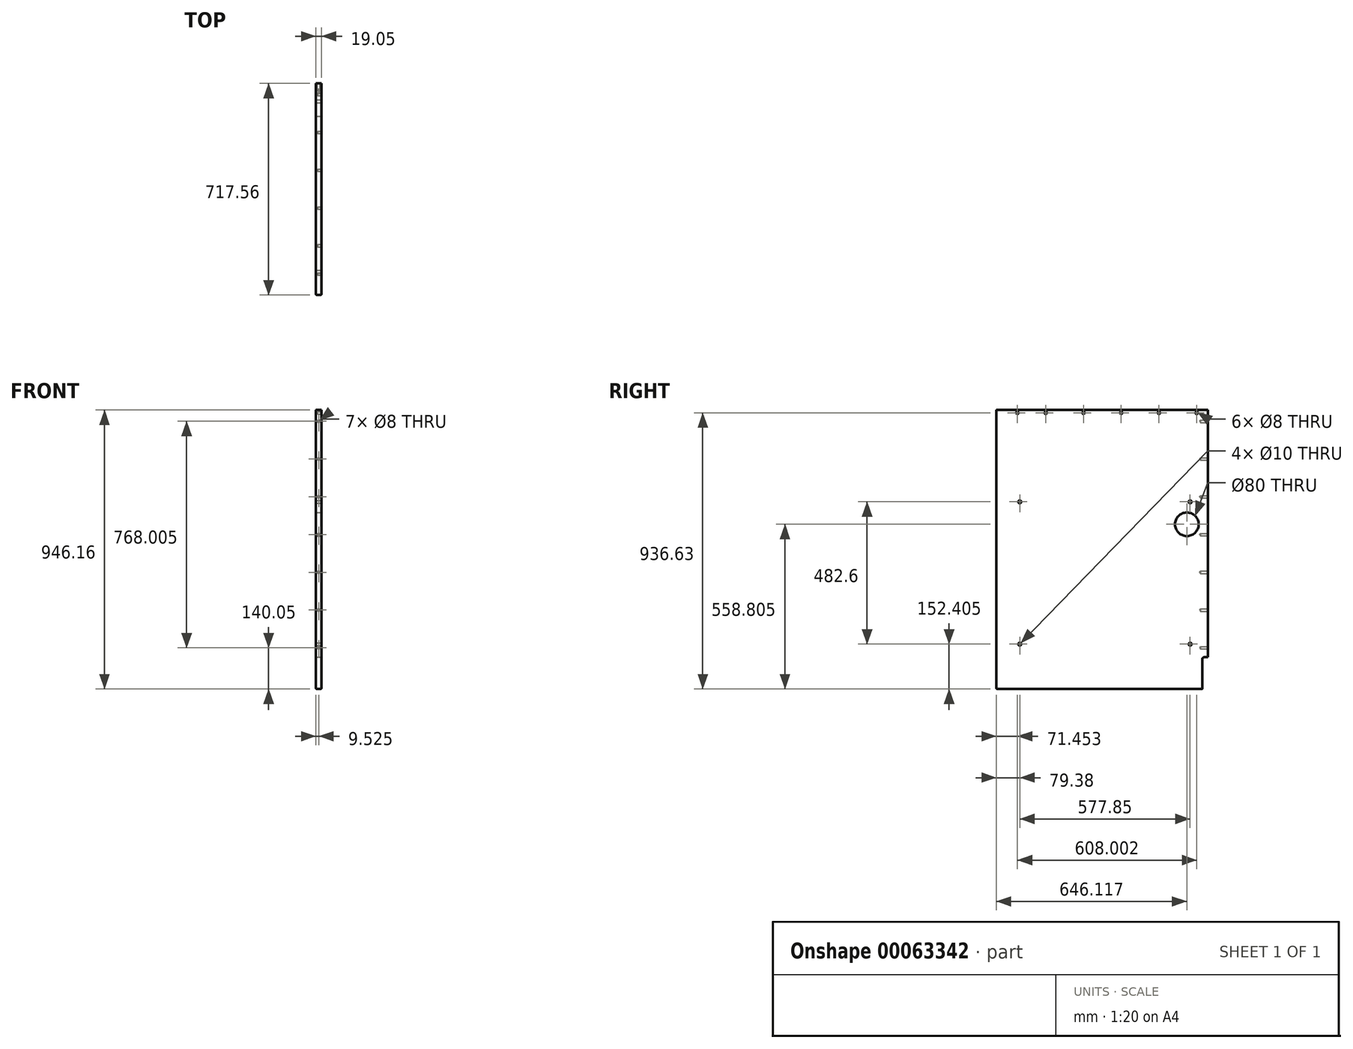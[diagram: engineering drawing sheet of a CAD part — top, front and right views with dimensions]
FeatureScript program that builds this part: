
annotation { "Feature Type Name" : "Feature", "Feature Type Description" : "" }
export const myFeature = defineFeature(function(context is Context, id is Id, definition is map)
    precondition{}
    {
        {
            var Q0;
            Q0=qCreatedBy(makeId("Right.planeOp"),FACE);
            var sketch = newSketch(context, id + "F0", { "sketchPlane" : qUnion([Q0])});
            skLineSegment(sketch, "E0.rect.bottom", {"start": v(358.78, -473.08) * mm, "end": v(-358.78, -473.08) * mm});
            skLineSegment(sketch, "E0.rect.top", {"start": v(358.78, 473.08) * mm, "end": v(-358.77, 473.07) * mm});
            skLineSegment(sketch, "E0.rect.left", {"start": v(358.78, -473.08) * mm, "end": v(358.78, 473.08) * mm});
            skLineSegment(sketch, "E0.rect.right", {"start": v(-358.78, -473.08) * mm, "end": v(-358.77, 473.08) * mm});
            skPoint(sketch, "E0.rect.middle", {"position": v(0, 0) * mm});
            skSolve(sketch);
        }
        {
            var Q0;
            Q0=makeQuery(id+"F0.imprint","IMPRINT",FACE,{"disambiguationData":[TD([[makeQuery(id+"F0.imprint","IMPRINT",EDGE,{"derivedFrom":sQuery(id+"F0.wireOp",EDGE,"E0.rect.bottom")}),-1.0]])]});
            extrude(context, id + "F1", {"entities" : qUnion([Q0]), "oppositeDirection" : true, "depth" : 19.05 * mm});
        }
        {
            var Q0;
            Q0=makeQuery(id+"F1.opExtrude","CAP_FACE",FACE,{"disambiguationData":[OSD([sQuery(id+"F0.wireOp",EDGE,"E0.rect.bottom"),sQuery(id+"F0.wireOp",EDGE,"E0.rect.top"),sQuery(id+"F0.wireOp",EDGE,"E0.rect.left"),sQuery(id+"F0.wireOp",EDGE,"E0.rect.right")])],"isStart":true});
            var sketch = newSketch(context, id + "F2", { "sketchPlane" : qUnion([Q0])});
            skPoint(sketch, "E1", {"position": v(320.68, 463.55) * mm});
            skPoint(sketch, "E2", {"position": v(192.67, 463.55) * mm});
            skPoint(sketch, "E3", {"position": v(64.67, 463.55) * mm});
            skPoint(sketch, "E4", {"position": v(-63.33, 463.55) * mm});
            skPoint(sketch, "E5", {"position": v(-191.33, 463.55) * mm});
            skPoint(sketch, "E6", {"position": v(-287.33, 463.55) * mm});
            skSolve(sketch);
        }
        {
            var Q0;
            Q0=sQuery(id+"F2.wireOp",VERTEX,"E6");
            var Q1;
            Q1=sQuery(id+"F2.wireOp",VERTEX,"E5");
            var Q2;
            Q2=sQuery(id+"F2.wireOp",VERTEX,"E4");
            var Q3;
            Q3=sQuery(id+"F2.wireOp",VERTEX,"E3");
            var Q4;
            Q4=sQuery(id+"F2.wireOp",VERTEX,"E2");
            var Q5;
            Q5=sQuery(id+"F2.wireOp",VERTEX,"E1");
            var Q6;
            Q6=makeQuery(id+"F1.opExtrude","SWEPT_BODY",BODY,{"disambiguationData":[OSD([sQuery(id+"F0.wireOp",EDGE,"E0.rect.bottom"),sQuery(id+"F0.wireOp",EDGE,"E0.rect.top"),sQuery(id+"F0.wireOp",EDGE,"E0.rect.left"),sQuery(id+"F0.wireOp",EDGE,"E0.rect.right")])]});
            hole(context, id + "F3", {"style" : HoleStyle.SIMPLE, "holeDiameter" : 8 * mm, "endStyle" : HoleEndStyle.BLIND, "holeDepth" : 12.7 * mm, "locations" : qUnion([Q0, Q1, Q2, Q3, Q4, Q5]), "scope" : qUnion([Q6])});
        }
        {
            var Q0;
            Q0=makeQuery(id+"F1.opExtrude","CAP_FACE",FACE,{"disambiguationData":[OSD([sQuery(id+"F0.wireOp",EDGE,"E0.rect.bottom"),sQuery(id+"F0.wireOp",EDGE,"E0.rect.top"),sQuery(id+"F0.wireOp",EDGE,"E0.rect.left"),sQuery(id+"F0.wireOp",EDGE,"E0.rect.right")])],"isStart":true});
            var sketch = newSketch(context, id + "F4", { "sketchPlane" : qUnion([Q0])});
            skLineSegment(sketch, "E7.bottom", {"start": v(358.78, -473.08) * mm, "end": v(339.73, -473.08) * mm});
            skLineSegment(sketch, "E7.top", {"start": v(358.78, -365.13) * mm, "end": v(346.08, -365.13) * mm});
            skLineSegment(sketch, "E7.left", {"start": v(358.78, -473.08) * mm, "end": v(358.78, -365.13) * mm});
            skLineSegment(sketch, "E7.right", {"start": v(339.73, -473.08) * mm, "end": v(339.73, -371.48) * mm});
            skPoint(sketch, "E8.visualSharp", {"position": v(339.73, -365.13) * mm});
            skArc(sketch, "E8.filletArc", {"start": v(346.08, -365.13) * mm, "mid": v(341.58, -366.98) * mm, "end": v(339.73, -371.48) * mm});
            skSolve(sketch);
        }
        {
            var Q0;
            Q0=makeQuery(id+"F4.imprint","IMPRINT",FACE,{"disambiguationData":[TD([[makeQuery(id+"F4.imprint","IMPRINT",EDGE,{"derivedFrom":sQuery(id+"F4.wireOp",EDGE,"E7.bottom")}),-1.0]])]});
            extrude(context, id + "F5", {"entities" : qUnion([Q0]), "operationType" : NewBodyOperationType.REMOVE, "endBound" : BoundingType.THROUGH_ALL, "oppositeDirection" : true, "depth" : 25.4 * mm});
        }
        {
            var Q0;
            Q0=makeQuery(id+"F1.opExtrude","CAP_FACE",FACE,{"disambiguationData":[OSD([sQuery(id+"F0.wireOp",EDGE,"E0.rect.bottom"),sQuery(id+"F0.wireOp",EDGE,"E0.rect.top"),sQuery(id+"F0.wireOp",EDGE,"E0.rect.left"),sQuery(id+"F0.wireOp",EDGE,"E0.rect.right")])],"isStart":true});
            var sketch = newSketch(context, id + "F6", { "sketchPlane" : qUnion([Q0])});
            skPoint(sketch, "E9", {"position": v(-279.4, 161.92) * mm});
            skPoint(sketch, "E10", {"position": v(298.45, 161.92) * mm});
            skPoint(sketch, "E11", {"position": v(298.45, -320.68) * mm});
            skPoint(sketch, "E12", {"position": v(-279.4, -320.68) * mm});
            skSolve(sketch);
        }
        {
            var Q0;
            Q0=sQuery(id+"F6.wireOp",VERTEX,"E9");
            var Q1;
            Q1=sQuery(id+"F6.wireOp",VERTEX,"E12");
            var Q2;
            Q2=sQuery(id+"F6.wireOp",VERTEX,"E11");
            var Q3;
            Q3=sQuery(id+"F6.wireOp",VERTEX,"E10");
            var Q4;
            Q4=makeQuery(id+"F1.opExtrude","SWEPT_BODY",BODY,{"disambiguationData":[OSD([sQuery(id+"F0.wireOp",EDGE,"E0.rect.bottom"),sQuery(id+"F0.wireOp",EDGE,"E0.rect.top"),sQuery(id+"F0.wireOp",EDGE,"E0.rect.left"),sQuery(id+"F0.wireOp",EDGE,"E0.rect.right")])]});
            hole(context, id + "F7", {"style" : HoleStyle.SIMPLE, "holeDiameter" : 10 * mm, "endStyle" : HoleEndStyle.THROUGH, "locations" : qUnion([Q0, Q1, Q2, Q3]), "scope" : qUnion([Q4])});
        }
        {
            var Q0;
            Q0=makeQuery(id+"F1.opExtrude","CAP_FACE",FACE,{"disambiguationData":[OSD([sQuery(id+"F0.wireOp",EDGE,"E0.rect.bottom"),sQuery(id+"F0.wireOp",EDGE,"E0.rect.top"),sQuery(id+"F0.wireOp",EDGE,"E0.rect.left"),sQuery(id+"F0.wireOp",EDGE,"E0.rect.right")])],"isStart":true});
            var sketch = newSketch(context, id + "F8", { "sketchPlane" : qUnion([Q0])});
            skPoint(sketch, "E13", {"position": v(287.34, 85.72) * mm});
            skSolve(sketch);
        }
        {
            var Q0;
            Q0=sQuery(id+"F8.wireOp",VERTEX,"E13");
            var Q1;
            Q1=makeQuery(id+"F1.opExtrude","SWEPT_BODY",BODY,{"disambiguationData":[OSD([sQuery(id+"F0.wireOp",EDGE,"E0.rect.bottom"),sQuery(id+"F0.wireOp",EDGE,"E0.rect.top"),sQuery(id+"F0.wireOp",EDGE,"E0.rect.left"),sQuery(id+"F0.wireOp",EDGE,"E0.rect.right")])]});
            hole(context, id + "F9", {"style" : HoleStyle.SIMPLE, "holeDiameter" : 80 * mm, "endStyle" : HoleEndStyle.THROUGH, "locations" : qUnion([Q0]), "scope" : qUnion([Q1])});
        }
        {
            var Q0;
            Q0=makeQuery(id+"F1.opExtrude","SWEPT_FACE",FACE,{"disambiguationData":[OSD([sQuery(id+"F0.wireOp",EDGE,"E0.rect.left")])]});
            var sketch = newSketch(context, id + "F10", { "sketchPlane" : qUnion([Q0])});
            skPoint(sketch, "E14", {"position": v(9.53, 434.98) * mm});
            skPoint(sketch, "E15", {"position": v(9.53, 306.97) * mm});
            skPoint(sketch, "E16", {"position": v(9.53, 178.97) * mm});
            skPoint(sketch, "E17", {"position": v(9.53, 50.97) * mm});
            skPoint(sketch, "E18", {"position": v(9.53, -77.03) * mm});
            skPoint(sketch, "E19", {"position": v(9.53, -205.03) * mm});
            skPoint(sketch, "E20", {"position": v(9.53, -333.03) * mm});
            skSolve(sketch);
        }
        {
            var Q0;
            Q0=sQuery(id+"F10.wireOp",VERTEX,"E14");
            var Q1;
            Q1=sQuery(id+"F10.wireOp",VERTEX,"E15");
            var Q2;
            Q2=sQuery(id+"F10.wireOp",VERTEX,"E16");
            var Q3;
            Q3=sQuery(id+"F10.wireOp",VERTEX,"E17");
            var Q4;
            Q4=sQuery(id+"F10.wireOp",VERTEX,"E18");
            var Q5;
            Q5=sQuery(id+"F10.wireOp",VERTEX,"E19");
            var Q6;
            Q6=sQuery(id+"F10.wireOp",VERTEX,"E20");
            var Q7;
            Q7=makeQuery(id+"F1.opExtrude","SWEPT_BODY",BODY,{"disambiguationData":[OSD([sQuery(id+"F0.wireOp",EDGE,"E0.rect.bottom"),sQuery(id+"F0.wireOp",EDGE,"E0.rect.top"),sQuery(id+"F0.wireOp",EDGE,"E0.rect.left"),sQuery(id+"F0.wireOp",EDGE,"E0.rect.right")])]});
            hole(context, id + "F11", {"style" : HoleStyle.SIMPLE, "holeDiameter" : 8 * mm, "endStyle" : HoleEndStyle.BLIND, "holeDepth" : 25.4 * mm, "locations" : qUnion([Q0, Q1, Q2, Q3, Q4, Q5, Q6]), "scope" : qUnion([Q7])});
        }
        {
            var Q0;
            Q0=makeQuery(id+"F1.opExtrude","CAP_EDGE",EDGE,{"disambiguationData":[OSD([sQuery(id+"F0.wireOp",EDGE,"E0.rect.right")])],"isStart":false});
            var Q1;
            Q1=makeQuery(id+"F1.opExtrude","CAP_EDGE",EDGE,{"disambiguationData":[OSD([sQuery(id+"F0.wireOp",EDGE,"E0.rect.right")])],"isStart":true});
            var Q2;
            Q2=makeQuery(id+"F1.opExtrude","CAP_EDGE",EDGE,{"disambiguationData":[OSD([sQuery(id+"F0.wireOp",EDGE,"E0.rect.bottom")])],"isStart":true});
            var Q3;
            Q3=makeQuery(id+"F1.opExtrude","CAP_EDGE",EDGE,{"disambiguationData":[OSD([sQuery(id+"F0.wireOp",EDGE,"E0.rect.bottom")])],"isStart":false});
            var Q4;
            Q4=makeQuery(id+"F1.opExtrude","SWEPT_EDGE",EDGE,{"disambiguationData":[OSD([sQuery(id+"F0.wireOp",EDGE,"E0.rect.bottom"),sQuery(id+"F0.wireOp",EDGE,"E0.rect.right")])]});
            fillet(context, id + "F12", {"entities" : qUnion([Q0, Q1, Q2, Q3, Q4]), "radius" : 3.17 * mm, "tangentPropagation" : true, "allowEdgeOverflow" : false});
        }
    });
